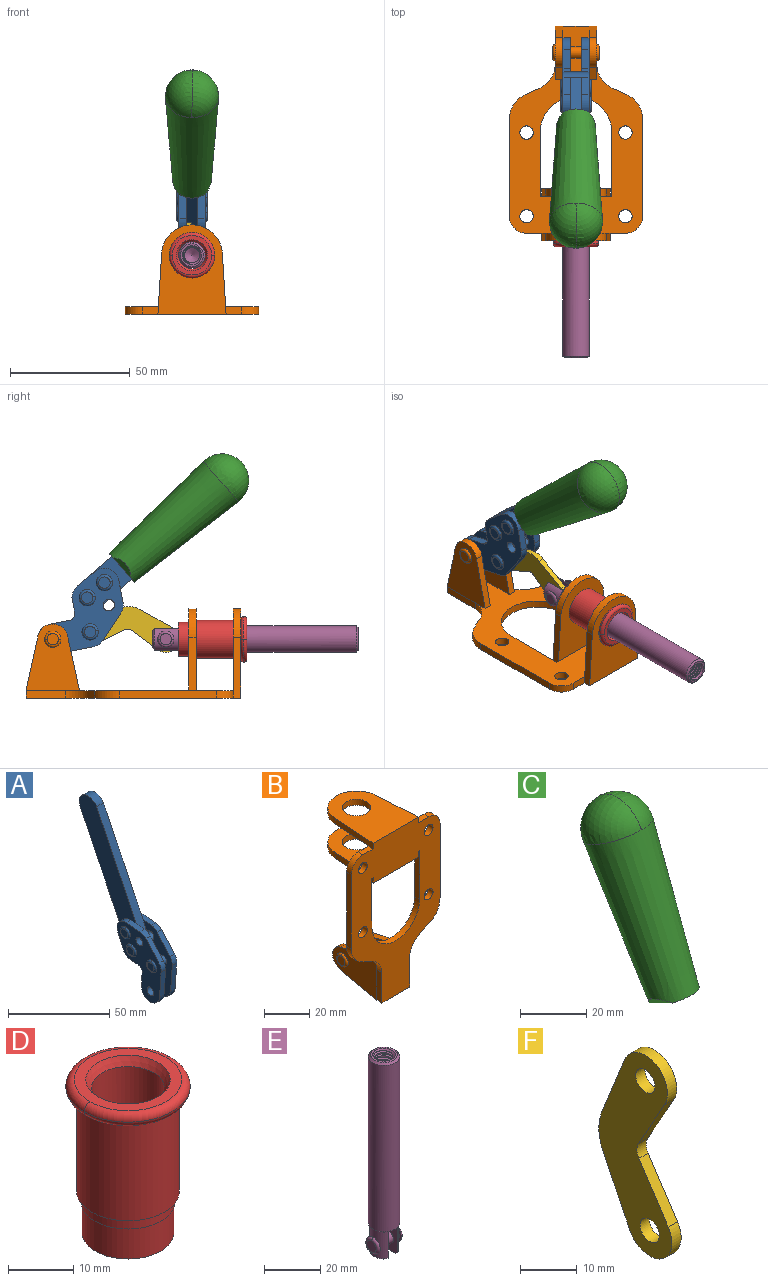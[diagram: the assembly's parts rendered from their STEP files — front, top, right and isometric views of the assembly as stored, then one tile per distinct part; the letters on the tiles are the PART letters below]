
ASSEMBLY  parts=6 mates=6
PART A: 59 faces, bbox 12.9x60.2x99.6 mm
  f0: torus R=2.39mm, axis (-1,0,0), area 14.9mm2, adj f20,f43,f51
  f1: torus R=2.39mm, axis (-1,0,0), area 14.9mm2, adj f19,f42,f51
  f2: torus R=2.39mm, axis (-1,0,0), area 14.9mm2, adj f18,f35,f51
  f3: torus R=2.39mm, axis (-1,0,0), area 14.9mm2, adj f14,f17,f23
  f4: torus R=2.39mm, axis (-1,0,0), area 14.9mm2, adj f13,f16,f23
  f5: torus R=2.39mm, axis (-1,0,0), area 14.9mm2, adj f12,f15,f23
  f6: cylinder r=2.39mm len=4.78mm, axis (1,0,0), area 46.5mm2, adj f48,f50,f51
  f7: cylinder r=2.39mm len=4.78mm, axis (1,0,0), area 46.5mm2, adj f50,f51
  f8: cylinder r=6.35mm len=12.68mm, axis (1,0,0), area 61.8mm2, adj f38,f39,f50,f51
  f9: cylinder r=2.39mm len=4.78mm, axis (-1,0,0), area 70.5mm2, adj f46,f50
  f10: cylinder r=2.39mm len=4.78mm, axis (-1,0,0), area 46.5mm2, adj f23,f45,f46
  f11: cylinder r=2.39mm len=4.78mm, axis (-1,0,0), area 46.5mm2, adj f23,f46
  f12: plane 4.78x4.78mm, normal (1,0,0), area 17.9mm2, adj f5,f15
  f13: plane 4.78x4.78mm, normal (1,0,0), area 17.9mm2, adj f4,f16
  f14: plane 4.78x4.78mm, normal (1,0,0), area 17.9mm2, adj f3,f17
  f15: torus R=2.39mm, axis (-1,0,0), area 14.9mm2, adj f5,f12,f23
  f16: torus R=2.39mm, axis (-1,0,0), area 14.9mm2, adj f4,f13,f23
  f17: torus R=2.39mm, axis (-1,0,0), area 14.9mm2, adj f3,f14,f23
  f18: plane 4.78x4.78mm, normal (-1,0,0), area 17.9mm2, adj f2,f35
  f19: plane 4.78x4.78mm, normal (-1,0,0), area 17.9mm2, adj f1,f42
  f20: plane 4.78x4.78mm, normal (-1,0,0), area 17.9mm2, adj f0,f43
  f21: plane 2.26x0.2mm, normal (1,0,0), area 0.2mm2, adj f31,f44
  f22: plane 2.26x0.2mm, normal (-1,0,0), area 0.2mm2, adj f41,f44
  f23: plane 39.37x30.77mm, normal (1,0,0), area 565.5mm2, adj f3,f4,f5,f10,f11,f15,f16,f17
  f24: cylinder r=6.1mm len=4.15mm, axis (-1,0,0), area 14.7mm2, adj f23,f25,f32,f46
  f25: plane 10.25x9.01mm, normal (0,-0.75,0.66), area 42.3mm2, adj f23,f24,f26,f46
  f26: cylinder r=6.35mm len=4.64mm, axis (-1,0,0), area 15.6mm2, adj f23,f25,f27,f46
  f27: plane 15.84x3.1mm, normal (0,-1,-0.07), area 49.2mm2, adj f23,f26,f28,f46
  f28: cylinder r=6.35mm len=12.68mm, axis (-1,0,0), area 61.8mm2, adj f23,f27,f29,f46
  f29: plane 8.11x3.1mm, normal (0,1,0.07), area 25.2mm2, adj f23,f28,f30,f46
  f30: cylinder r=3.05mm len=3.25mm, axis (-1,0,0), area 14.8mm2, adj f23,f29,f31,f46
  f31: plane 5.99x3.1mm, normal (0,0.07,-1), area 18.6mm2, adj f21,f23,f30,f44,f46
  f32: plane 9.5x3.1mm, normal (0,-0.07,1), area 29.5mm2, adj f23,f24,f33,f46,f47
  f33: cylinder r=6.1mm len=8.63mm, axis (-1,0,0), area 39.1mm2, adj f23,f32,f34,f47
  f34: plane 8.65x3.96mm, normal (0,0.91,-0.42), area 29.5mm2, adj f23,f33,f44,f47
  f35: torus R=2.39mm, axis (-1,0,0), area 14.9mm2, adj f2,f18,f51
  f36: plane 10.25x9.01mm, normal (0,-0.75,0.66), area 42.3mm2, adj f37,f49,f50,f51
  f37: cylinder r=6.35mm len=4.64mm, axis (1,0,0), area 15.6mm2, adj f36,f38,f50,f51
  f38: plane 15.84x3.1mm, normal (0,-1,-0.07), area 49.2mm2, adj f8,f37,f50,f51
  f39: plane 8.11x3.1mm, normal (0,1,0.07), area 25.2mm2, adj f8,f40,f50,f51
  f40: cylinder r=3.05mm len=3.25mm, axis (1,0,0), area 14.8mm2, adj f39,f41,f50,f51
  f41: plane 5.99x3.1mm, normal (0,0.07,-1), area 18.6mm2, adj f22,f40,f44,f50,f51
  f42: torus R=2.39mm, axis (-1,0,0), area 14.9mm2, adj f1,f19,f51
  f43: torus R=2.39mm, axis (-1,0,0), area 14.9mm2, adj f0,f20,f51
  f44: cylinder r=6.35mm len=12.12mm, axis (-1,0,0), area 128.9mm2, adj f21,f22,f23,f31,f34,f41,f46,f47
  f45: plane 2.65x1.35mm, normal (1,0,0), area 1mm2, adj f10,f55
  f46: plane 39.08x20.42mm, normal (-1,0,0), area 412.5mm2, adj f9,f10,f11,f24,f25,f26,f27,f28
  f47: plane 77.62x39.82mm, normal (1,0,0), area 850mm2, adj f32,f33,f34,f44,f53,f54,f55
  f48: plane 2.65x1.35mm, normal (-1,0,0), area 1mm2, adj f6,f55
  f49: cylinder r=6.1mm len=4.15mm, axis (1,0,0), area 14.7mm2, adj f36,f50,f51,f56
  f50: plane 39.08x20.42mm, normal (1,0,0), area 412.5mm2, adj f6,f7,f8,f9,f36,f37,f38,f39
  f51: plane 39.37x30.77mm, normal (-1,0,0), area 565.5mm2, adj f0,f1,f2,f6,f7,f8,f35,f36
  f52: plane 8.65x3.96mm, normal (0,0.91,-0.42), area 29.5mm2, adj f44,f51,f57,f58
  f53: plane 68.49x33.4mm, normal (0,0.9,-0.44), area 358.1mm2, adj f44,f47,f54,f58
  f54: cylinder r=6.35mm len=12.06mm, axis (1,0,0), area 93.7mm2, adj f47,f53,f55,f58
  f55: plane 68.49x33.4mm, normal (0,-0.9,0.44), area 358.1mm2, adj f44,f45,f46,f47,f48,f50,f54,f58
  f56: plane 9.5x3.1mm, normal (0,-0.07,1), area 29.5mm2, adj f49,f50,f51,f57,f58
  f57: cylinder r=6.1mm len=8.63mm, axis (1,0,0), area 39.1mm2, adj f51,f52,f56,f58
  f58: plane 77.62x39.82mm, normal (-1,0,0), area 850mm2, adj f44,f52,f53,f54,f55,f56,f57
PART B: 55 faces, bbox 55.7x37.4x89.8 mm
  f0: torus R=2.41mm, axis (-1,0,0), area 15mm2, adj f11,f15,f25
  f1: torus R=2.41mm, axis (-1,0,0), area 15mm2, adj f10,f12,f22
  f2: cylinder r=2.78mm len=5.56mm, axis (0,-1,0), area 54.2mm2, adj f30,f54
  f3: cylinder r=14.99mm len=29.97mm, axis (0,-1,0), area 145.9mm2, adj f30,f49,f53,f54
  f4: cylinder r=2.78mm len=5.56mm, axis (0,-1,0), area 54.2mm2, adj f30,f54
  f5: cylinder r=2.78mm len=5.56mm, axis (0,-1,0), area 54.2mm2, adj f30,f54
  f6: cylinder r=2.78mm len=5.56mm, axis (0,-1,0), area 54.2mm2, adj f30,f54
  f7: cylinder r=6.35mm len=12.7mm, axis (0,0,1), area 123.6mm2, adj f27,f51
  f8: cylinder r=6.35mm len=12.7mm, axis (0,0,-1), area 124.7mm2, adj f21,f35
  f9: cylinder r=2.41mm len=11.18mm, axis (-1,0,0), area 169.4mm2, adj f16,f19
  f10: plane 4.83x4.83mm, normal (1,0,0), area 18.3mm2, adj f1,f12
  f11: plane 4.83x4.83mm, normal (-1,0,0), area 18.3mm2, adj f0,f15
  f12: torus R=2.41mm, axis (-1,0,0), area 15mm2, adj f1,f10,f22
  f13: cylinder r=6.35mm len=12.41mm, axis (1,0,0), area 53.4mm2, adj f18,f19,f22,f23
  f14: cylinder r=6.35mm len=12.41mm, axis (-1,0,0), area 53.4mm2, adj f16,f17,f24,f25
  f15: torus R=2.41mm, axis (-1,0,0), area 15mm2, adj f0,f11,f25
  f16: plane 27.86x22.35mm, normal (1,0,0), area 425.4mm2, adj f9,f14,f17,f24,f30
  f17: plane 22.86x4.97mm, normal (0,0.21,0.98), area 72.5mm2, adj f14,f16,f25,f30
  f18: plane 22.86x4.97mm, normal (0,0.21,0.98), area 72.5mm2, adj f13,f19,f22,f30
  f19: plane 27.86x22.35mm, normal (-1,0,0), area 425.4mm2, adj f9,f13,f18,f23,f30
  f20: cylinder r=12.7mm len=25.35mm, axis (0,0,-1), area 119.8mm2, adj f21,f34,f35,f36
  f21: plane 34.21x28.07mm, normal (0,0,-1), area 702.4mm2, adj f8,f20,f30,f34,f36
  f22: plane 27.96x22.45mm, normal (1,0,0), area 407.2mm2, adj f1,f12,f13,f18,f23,f30,f42,f43
  f23: plane 22.86x4.97mm, normal (0,0.21,-0.98), area 72.5mm2, adj f13,f19,f22,f44
  f24: plane 22.86x4.97mm, normal (0,0.21,-0.98), area 72.5mm2, adj f14,f16,f25,f44
  f25: plane 27.86x22.35mm, normal (-1,0,0), area 407.1mm2, adj f0,f14,f15,f17,f24,f30,f45,f46
  f26: plane 3.1x0.95mm, normal (0,0,-1), area 2.7mm2, adj f30,f49,f50,f54
  f27: plane 34.21x28.07mm, normal (0,0,1), area 702.4mm2, adj f7,f28,f30,f50,f52
  f28: cylinder r=12.7mm len=25.35mm, axis (0,0,1), area 118.8mm2, adj f27,f50,f51,f52
  f29: plane 3.1x0.95mm, normal (0,0,-1), area 2.7mm2, adj f30,f52,f53,f54
  f30: plane 86.54x55.63mm, normal (0,1,0), area 2362.9mm2, adj f2,f3,f4,f5,f6,f16,f17,f18
  f31: plane 40.56x3.1mm, normal (-1,0,0), area 125.7mm2, adj f30,f32,f48,f54
  f32: cylinder r=7.11mm len=7.11mm, axis (0,-1,0), area 34.6mm2, adj f30,f31,f33,f54
  f33: plane 6.67x3.1mm, normal (0,0,1), area 20.4mm2, adj f30,f32,f34,f54
  f34: plane 25.39x3.13mm, normal (-1,0.06,0), area 79.5mm2, adj f20,f21,f33,f35,f54
  f35: plane 37.31x28.45mm, normal (0,0,1), area 789.9mm2, adj f8,f20,f34,f36,f54
  f36: plane 25.39x3.13mm, normal (1,0.06,0), area 79.5mm2, adj f20,f21,f35,f37,f54
  f37: plane 6.67x3.1mm, normal (0,0,1), area 20.4mm2, adj f30,f36,f38,f54
  f38: cylinder r=7.11mm len=7.11mm, axis (0,-1,0), area 34.6mm2, adj f30,f37,f39,f54
  f39: plane 40.56x3.1mm, normal (1,0,0), area 125.7mm2, adj f30,f38,f40,f54
  f40: cylinder r=11.18mm len=10.16mm, axis (0,-1,0), area 39.5mm2, adj f30,f39,f41,f54
  f41: plane 6.09x3.1mm, normal (0.42,0,-0.91), area 20.8mm2, adj f30,f40,f42,f54
  f42: cylinder r=11.18mm len=9.41mm, axis (0,-1,0), area 37.2mm2, adj f22,f30,f41,f43,f54
  f43: plane 16.5x3.1mm, normal (1,0,0), area 51.1mm2, adj f22,f42,f44,f54
  f44: plane 17.37x3.1mm, normal (0,0,-1), area 53.8mm2, adj f23,f24,f30,f43,f45,f54
  f45: plane 16.5x3.1mm, normal (-1,0,0), area 51.1mm2, adj f25,f44,f46,f54
  f46: cylinder r=11.18mm len=9.41mm, axis (0,-1,0), area 37.2mm2, adj f25,f30,f45,f47,f54
  f47: plane 6.09x3.1mm, normal (-0.42,0,-0.91), area 20.8mm2, adj f30,f46,f48,f54
  f48: cylinder r=11.18mm len=10.16mm, axis (0,-1,0), area 39.5mm2, adj f30,f31,f47,f54
  f49: plane 26.54x3.1mm, normal (-1,0,0), area 82.3mm2, adj f3,f26,f30,f54
  f50: plane 25.39x3.1mm, normal (1,0.06,0), area 78.8mm2, adj f26,f27,f28,f51,f54
  f51: plane 37.31x28.45mm, normal (0,0,-1), area 789.9mm2, adj f7,f28,f50,f52,f54
  f52: plane 25.39x3.1mm, normal (-1,0.06,0), area 78.8mm2, adj f27,f28,f29,f51,f54
  f53: plane 26.54x3.1mm, normal (1,0,0), area 82.3mm2, adj f3,f29,f30,f54
  f54: plane 89.66x55.63mm, normal (0,-1,0), area 2678.5mm2, adj f2,f3,f4,f5,f6,f26,f29,f31
PART C: 11 faces, bbox 22.3x42.6x64.5 mm
  f0: sphere r=11.13mm, area 411.4mm2, adj f1,f8
  f1: cone r=11.11mm half-angle=3.3deg, axis (0,0.44,0.9), area 3251.8mm2, adj f0,f7,f8,f9,f10
  f2: cylinder r=6.16mm len=11.7mm, axis (1,0,0), area 89.5mm2, adj f3,f4,f5,f6
  f3: plane 60.23x36.75mm, normal (-1,0,0), area 763.6mm2, adj f2,f4,f6,f10
  f4: plane 51.37x25.05mm, normal (0,0.9,-0.44), area 264.2mm2, adj f2,f3,f5,f10
  f5: plane 60.23x36.75mm, normal (1,0,0), area 763.6mm2, adj f2,f4,f6,f10
  f6: plane 51.37x25.05mm, normal (0,-0.9,0.44), area 264.2mm2, adj f2,f3,f5,f10
  f7: plane 9.95x5.95mm, normal (0.71,-0.31,-0.64), area 25.8mm2, adj f1,f10
  f8: sphere r=11.13mm, area 411.4mm2, adj f0,f1
  f9: plane 9.95x5.95mm, normal (-0.71,-0.31,-0.64), area 25.8mm2, adj f1,f10
  f10: plane 14.27x11.38mm, normal (0,-0.44,-0.9), area 106.7mm2, adj f1,f3,f4,f5,f6,f7,f9
PART D: 15 faces, bbox 20.6x20.6x28.7 mm
  f0: torus R=8.26mm, axis (0,0,1), area 56.8mm2, adj f1,f10,f12
  f1: torus R=8.26mm, axis (0,0,1), area 56.8mm2, adj f0,f6,f13
  f2: cylinder r=5.59mm len=25.91mm, axis (0,0,1), area 909.6mm2, adj f3,f4
  f3: cone r=6.86mm half-angle=45deg, axis (0,0,-1), area 70.2mm2, adj f2,f14
  f4: cone r=6.47mm half-angle=30deg, axis (0,0,1), area 66.7mm2, adj f2,f13
  f5: cylinder r=7.04mm len=14.07mm, axis (0,0,1), area 252.6mm2, adj f11,f14
  f6: torus R=8.26mm, axis (0,0,1), area 56.8mm2, adj f1,f12,f13
  f7: cylinder r=7.16mm len=14.33mm, axis (0,0,1), area 91.5mm2, adj f9,f11
  f8: cylinder r=7.86mm len=18.42mm, axis (0,0,1), area 909.6mm2, adj f9,f10
  f9: plane 15.72x15.72mm, normal (0,0,-1), area 33mm2, adj f7,f8
  f10: plane 16.51x16.51mm, normal (0,0,-1), area 19.9mm2, adj f0,f8,f12
  f11: plane 14.33x14.33mm, normal (0,0,-1), area 5.7mm2, adj f5,f7
  f12: torus R=8.26mm, axis (0,0,1), area 56.8mm2, adj f0,f6,f10
  f13: plane 16.51x16.51mm, normal (0,0,1), area 82.7mm2, adj f1,f4,f6
  f14: plane 14.07x14.07mm, normal (0,0,-1), area 7.8mm2, adj f3,f5
PART E: 48 faces, bbox 12.6x11.1x86.1 mm
  f0: torus R=2.41mm, axis (-1,0,0), area 15mm2, adj f30,f32,f34
  f1: torus R=2.41mm, axis (-1,0,0), area 15mm2, adj f29,f31,f33
  f2: cylinder r=5.54mm len=72.39mm, axis (0,0,1), area 2518.5mm2, adj f3,f4,f42,f43
  f3: cone r=5.54mm half-angle=45deg, axis (0,0,1), area 7.6mm2, adj f2,f5,f41
  f4: cone r=5.54mm half-angle=45deg, axis (0,0,-1), area 34.9mm2, adj f2,f39
  f5: cylinder r=5.08mm len=11.48mm, axis (0,0,1), area 108.3mm2, adj f3,f7,f8,f41
  f6: cylinder r=2.41mm len=4.83mm, axis (-1,0,0), area 71.2mm2, adj f40,f41
  f7: cylinder r=2.41mm len=4.83mm, axis (-1,0,0), area 7.6mm2, adj f5,f34
  f8: cone r=5.08mm half-angle=45deg, axis (0,0,1), area 10.6mm2, adj f5,f37,f41
  f9: cone r=3.98mm half-angle=45deg, axis (0,0,1), area 17.6mm2, adj f27,f39,f45,f46,f47
  f10: cylinder r=2.41mm len=4.83mm, axis (-1,0,0), area 7.6mm2, adj f33,f38
  f11: cylinder r=3.2mm len=6.4mm, axis (0,0,1), area 78.4mm2, adj f12,f28,f44,f45,f47
  f12: cylinder r=3.2mm len=6.4mm, axis (0,0,1), area 10.5mm2, adj f11,f13,f45,f47
  f13: cylinder r=3.2mm len=6.4mm, axis (0,0,1), area 10.5mm2, adj f12,f14,f45,f47
  f14: cylinder r=3.2mm len=6.4mm, axis (0,0,1), area 10.5mm2, adj f13,f15,f45,f47
  f15: cylinder r=3.2mm len=6.4mm, axis (0,0,1), area 10.5mm2, adj f14,f16,f45,f47
  f16: cylinder r=3.2mm len=6.4mm, axis (0,0,1), area 10.5mm2, adj f15,f17,f45,f47
  f17: cylinder r=3.2mm len=6.4mm, axis (0,0,1), area 10.5mm2, adj f16,f18,f45,f47
  f18: cylinder r=3.2mm len=6.4mm, axis (0,0,1), area 10.5mm2, adj f17,f19,f45,f47
  f19: cylinder r=3.2mm len=6.4mm, axis (0,0,1), area 10.5mm2, adj f18,f20,f45,f47
  f20: cylinder r=3.2mm len=6.4mm, axis (0,0,1), area 10.5mm2, adj f19,f21,f45,f47
  f21: cylinder r=3.2mm len=6.4mm, axis (0,0,1), area 10.5mm2, adj f20,f22,f45,f47
  f22: cylinder r=3.2mm len=6.4mm, axis (0,0,1), area 10.5mm2, adj f21,f23,f45,f47
  f23: cylinder r=3.2mm len=6.4mm, axis (0,0,1), area 10.5mm2, adj f22,f24,f45,f47
  f24: cylinder r=3.2mm len=6.4mm, axis (0,0,1), area 10.5mm2, adj f23,f25,f45,f47
  f25: cylinder r=3.2mm len=6.4mm, axis (0,0,1), area 10.5mm2, adj f24,f26,f45,f47
  f26: cylinder r=3.2mm len=6.4mm, axis (0,0,1), area 10.5mm2, adj f25,f27,f45,f47
  f27: cylinder r=3.2mm len=6.4mm, axis (0,0,1), area 7.4mm2, adj f9,f26,f45,f47
  f28: cone r=3.2mm half-angle=60deg, axis (0,0,1), area 37.2mm2, adj f11
  f29: plane 4.83x4.83mm, normal (-1,0,0), area 18.3mm2, adj f1,f31
  f30: plane 4.83x4.83mm, normal (1,0,0), area 18.3mm2, adj f0,f32
  f31: torus R=2.41mm, axis (-1,0,0), area 15mm2, adj f1,f29,f33
  f32: torus R=2.41mm, axis (-1,0,0), area 15mm2, adj f0,f30,f34
  f33: plane 6.83x6.83mm, normal (1,0,0), area 18.3mm2, adj f1,f10,f31
  f34: plane 6.83x6.83mm, normal (-1,0,0), area 18.3mm2, adj f0,f7,f32
  f35: cone r=5.08mm half-angle=45deg, axis (0,0,1), area 10.6mm2, adj f36,f38,f40
  f36: plane 7.25x1.97mm, normal (0,0,-1), area 10mm2, adj f35,f40
  f37: plane 7.25x1.97mm, normal (0,0,-1), area 10mm2, adj f8,f41
  f38: cylinder r=5.08mm len=11.48mm, axis (0,0,1), area 108.3mm2, adj f10,f35,f40,f42
  f39: plane 9.55x9.55mm, normal (0,0,1), area 22mm2, adj f4,f9
  f40: plane 12.76x10.09mm, normal (1,0,0), area 95.7mm2, adj f6,f35,f36,f38,f42,f43
  f41: plane 12.76x10.09mm, normal (-1,0,0), area 95.7mm2, adj f3,f5,f6,f8,f37,f43
  f42: cone r=5.54mm half-angle=45deg, axis (0,0,1), area 7.6mm2, adj f2,f38,f40
  f43: plane 11.07x4.7mm, normal (0,0,-1), area 50.4mm2, adj f2,f40,f41
  f44: plane 0.89x0.62mm, normal (-1,0,0), area 0.3mm2, adj f11,f45,f46,f47
  f45: bspline ~24.8x7.63mm, area 266.6mm2, adj f9,f11,f12,f13,f14,f15,f16,f17
  f46: bspline ~24.87x7.63mm, area 73.6mm2, adj f9,f44,f45,f47
  f47: bspline ~24.98x7.63mm, area 272.5mm2, adj f9,f11,f12,f13,f14,f15,f16,f17
PART F: 12 faces, bbox 2.3x18.2x42.8 mm
  f0: cylinder r=2.4mm len=4.8mm, axis (1,0,0), area 34.9mm2, adj f4,f11
  f1: cylinder r=10.41mm len=8.47mm, axis (1,0,0), area 20.2mm2, adj f4,f9,f10,f11
  f2: cylinder r=3.05mm len=3.16mm, axis (1,0,0), area 7.7mm2, adj f4,f6,f7,f11
  f3: cylinder r=2.4mm len=4.8mm, axis (1,0,0), area 34.9mm2, adj f4,f11
  f4: plane 42.81x18.23mm, normal (-1,0,0), area 414.1mm2, adj f0,f1,f2,f3,f5,f6,f7,f8
  f5: cylinder r=5.54mm len=10.67mm, axis (1,0,0), area 41.8mm2, adj f4,f6,f10,f11
  f6: plane 11.66x6.53mm, normal (0,-0.87,-0.49), area 30.9mm2, adj f2,f4,f5,f11
  f7: plane 11.17x7.33mm, normal (0,-0.84,0.55), area 30.9mm2, adj f2,f4,f8,f11
  f8: cylinder r=5.54mm len=10.51mm, axis (1,0,0), area 41.8mm2, adj f4,f7,f9,f11
  f9: plane 13.67x6.67mm, normal (0,0.9,-0.44), area 35.1mm2, adj f1,f4,f8,f11
  f10: plane 14.1x5.7mm, normal (0,0.93,0.37), area 35.1mm2, adj f1,f4,f5,f11
  f11: plane 42.81x18.23mm, normal (1,0,0), area 414.1mm2, adj f0,f1,f2,f3,f5,f6,f7,f8
PLACE A rot(axis=(1,0,0),75deg) t=(0,4.15,9.14)mm
PLACE B rot(axis=(1,0,0),90deg) t=(0,9.43,0)mm fixed
PLACE C rot(axis=(1,0,0),75deg) t=(0,4.15,9.14)mm
PLACE D rot(axis=(1,0,0),90deg) t=(0,9.43,0)mm
PLACE E rot(axis=(1,0,0),90deg) t=(0,9.81,0)mm
PLACE F rot(axis=(1,0,0),97.5deg) t=(-1.16,12.88,2.22)mm
MATE revolute B.f0 <-> A.f7  axis (-1,0,0) through (0,41.52,24.61)mm
MATE revolute F.f3 <-> A.f4  axis (1,0,0) through (0,25.94,27.64)mm
MATE revolute E.f6 <-> F.f5  axis (-1,0,0) through (0,-5.67,24.61)mm
MATE slider E.f2 <-> D.f2  axis (0,-1,0) through (0,-48.97,24.61)mm
MATE fastened B.f7 <-> D.f2  axis (0,-1,0) through (0,-36.96,24.61)mm
MATE fastened A.f54 <-> C.f2  axis (1,0,0) through (0,-30.37,91.94)mm
